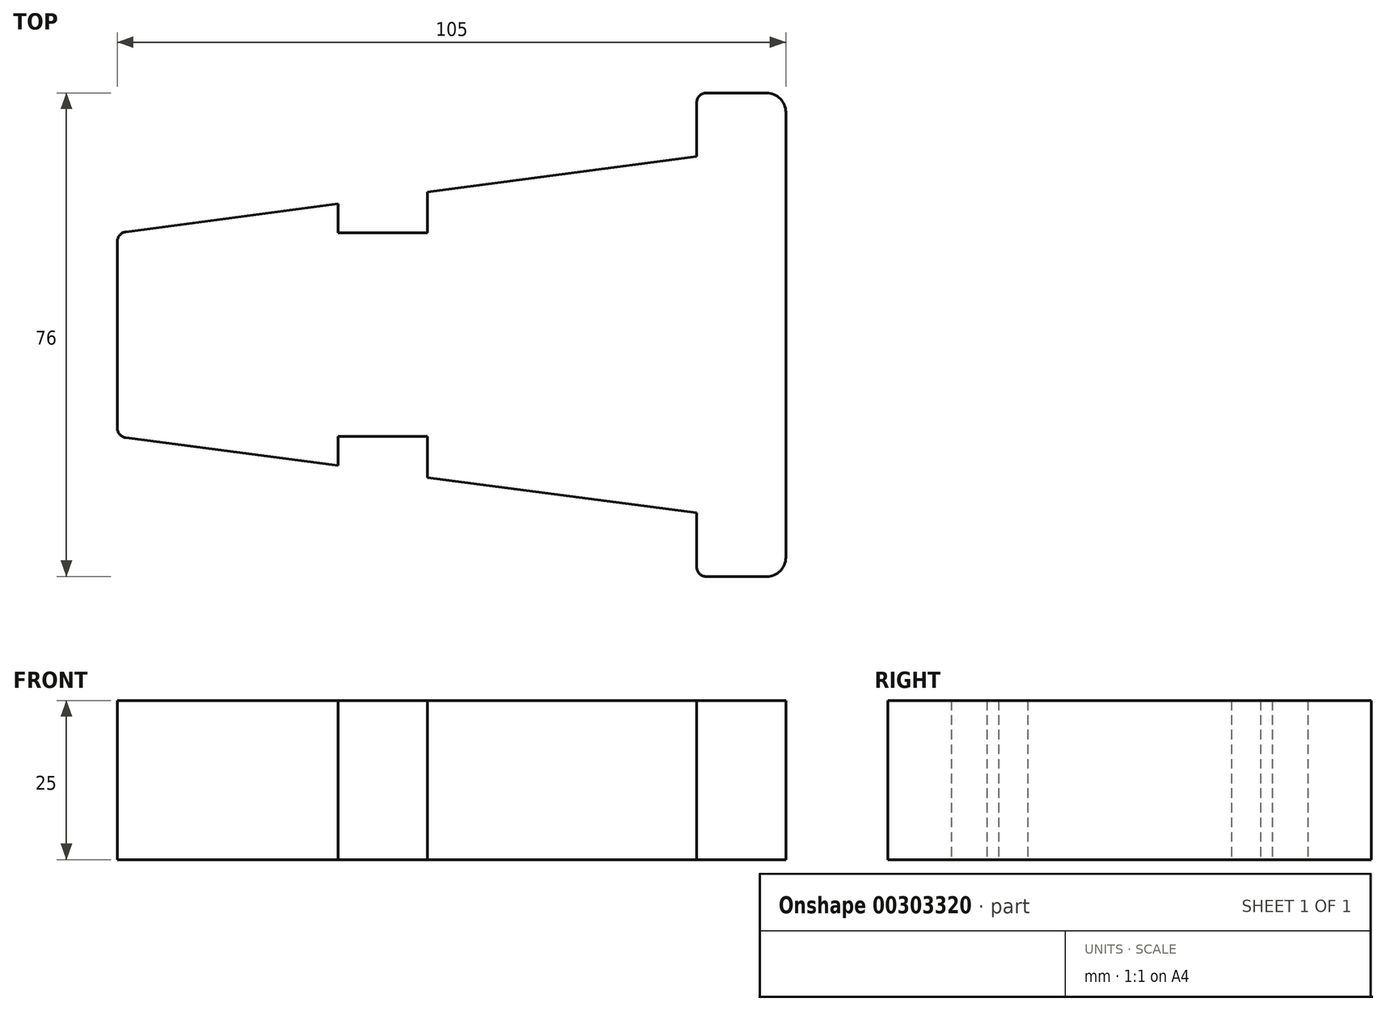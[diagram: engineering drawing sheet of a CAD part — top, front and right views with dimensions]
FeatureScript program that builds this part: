
annotation { "Feature Type Name" : "Feature", "Feature Type Description" : "" }
export const myFeature = defineFeature(function(context is Context, id is Id, definition is map)
    precondition{}
    {
        {
            var Q0;
            Q0=qCreatedBy(makeId("Top.planeOp"),FACE);
            var sketch = newSketch(context, id + "F0", { "sketchPlane" : qUnion([Q0])});
            skLineSegment(sketch, "E0", {"start": v(56.3, 49.66) * mm, "end": v(56.3, -20.34) * mm});
            skLineSegment(sketch, "E1", {"start": v(53.3, -23.34) * mm, "end": v(43.8, -23.34) * mm});
            skLineSegment(sketch, "E2", {"start": v(53.3, 52.66) * mm, "end": v(43.8, 52.66) * mm});
            skLineSegment(sketch, "E3", {"start": v(42.3, 51.16) * mm, "end": v(42.3, 42.66) * mm});
            skLineSegment(sketch, "E4", {"start": v(42.3, -21.84) * mm, "end": v(42.3, -13.34) * mm});
            skLineSegment(sketch, "E5", {"start": v(-48.7, 14.66) * mm, "end": v(-48.7, 29.34) * mm});
            skLineSegment(sketch, "E6", {"start": v(-48.7, 14.66) * mm, "end": v(-48.7, -0.02) * mm});
            skLineSegment(sketch, "E7", {"start": v(-48.7, 30.66) * mm, "end": v(-14, 35.24) * mm});
            skPoint(sketch, "E8.end.orphan", {"position": v(0, 14.66) * mm});
            skLineSegment(sketch, "E9", {"start": v(42.3, -13.34) * mm, "end": v(0, -7.76) * mm});
            skLineSegment(sketch, "E10", {"start": v(-47.4, 30.83) * mm, "end": v(-14, 35.24) * mm});
            skLineSegment(sketch, "E11", {"start": v(-14, 35.24) * mm, "end": v(-14, 30.66) * mm});
            skLineSegment(sketch, "E12", {"start": v(-14, 30.66) * mm, "end": v(0, 30.66) * mm});
            skLineSegment(sketch, "E13", {"start": v(-14, -1.34) * mm, "end": v(0, -1.34) * mm});
            skLineSegment(sketch, "E14", {"start": v(0, -1.34) * mm, "end": v(0, -7.76) * mm});
            skLineSegment(sketch, "E15", {"start": v(0, 30.66) * mm, "end": v(0, 37.08) * mm});
            skLineSegment(sketch, "E16.trimOffspring", {"start": v(-14, -1.34) * mm, "end": v(-14, -5.92) * mm});
            skPoint(sketch, "E17.start.orphan", {"position": v(56.3, 14.66) * mm});
            skPoint(sketch, "E18.trimOffspring.start.orphan", {"position": v(-14, 14.66) * mm});
            skLineSegment(sketch, "E19.trimOffspring", {"start": v(0, 37.08) * mm, "end": v(42.3, 42.66) * mm});
            skLineSegment(sketch, "E20.trimOffspring", {"start": v(-14, -5.92) * mm, "end": v(-47.4, -1.51) * mm});
            skPoint(sketch, "E21.visualSharp", {"position": v(42.3, 52.66) * mm});
            skArc(sketch, "E21.filletArc", {"start": v(43.8, 52.66) * mm, "mid": v(42.74, 52.22) * mm, "end": v(42.3, 51.16) * mm});
            skPoint(sketch, "E22.visualSharp", {"position": v(56.3, 52.66) * mm});
            skArc(sketch, "E22.filletArc", {"start": v(56.3, 49.66) * mm, "mid": v(55.42, 51.78) * mm, "end": v(53.3, 52.66) * mm});
            skPoint(sketch, "E23.visualSharp", {"position": v(42.3, -23.34) * mm});
            skArc(sketch, "E23.filletArc", {"start": v(42.3, -21.84) * mm, "mid": v(42.74, -22.9) * mm, "end": v(43.8, -23.34) * mm});
            skPoint(sketch, "E24.visualSharp", {"position": v(56.3, -23.34) * mm});
            skArc(sketch, "E24.filletArc", {"start": v(53.3, -23.34) * mm, "mid": v(55.42, -22.46) * mm, "end": v(56.3, -20.34) * mm});
            skPoint(sketch, "E25.visualSharp", {"position": v(-48.7, 30.66) * mm});
            skArc(sketch, "E25.filletArc", {"start": v(-47.4, 30.83) * mm, "mid": v(-48.33, 30.33) * mm, "end": v(-48.7, 29.34) * mm});
            skPoint(sketch, "E26.visualSharp", {"position": v(-48.7, -1.34) * mm});
            skArc(sketch, "E26.filletArc", {"start": v(-48.7, -0.02) * mm, "mid": v(-48.33, -1.01) * mm, "end": v(-47.4, -1.51) * mm});
            skSolve(sketch);
        }
        {
            var Q0;
            Q0=makeQuery(id+"F0.imprint","IMPRINT",FACE,{"disambiguationData":[TD([[makeQuery(id+"F0.imprint","IMPRINT",EDGE,{"derivedFrom":sQuery(id+"F0.wireOp",EDGE,"E0")}),-1.0]])]});
            extrude(context, id + "F1", {"entities" : qUnion([Q0]), "depth" : 25 * mm});
        }
    });
